# Revit family: Practibox_S_flush_mounting_cabinet_12_modules_réf_135361_to_135414
name_source: partatom
category: Equipement électrique
revit_build: Autodesk Revit 2018 (Build: 20170223_1515(x64)
units: mm (PartAtom-declared; Revit-internal decimal feet)

## family parameters
Basée sur le plan de construction = Non
Configuration du panneau = Deux colonnes, circuits au sein
Cote de connecteur circulaire = Utiliser le diamètre
Couper avec des vides une fois chargée = Non
Numéro OmniClass = 23.80.30.11.17
Partagée = Non
Point de calcul de pièce = Non
Titre OmniClass = Distribution Boards and Control Panels
Toujours verticalement = Oui
Type d'élément = Tableau de raccordement

## types (16) — shared parameters
Fabricant = "Legrand"
General Conditions of Use = https://export.legrand.com
URL = www.legrand.com
width = 328 mm  [stored 1.07612 ft]

## per-type parameters (varying)
| type | 1R | 2R | 3R | 4R | Ina | Terminal block E | Terminal block N | depth | door B 1 r | door B 2 r | door B 3 r | door B 4 r | door T 1 r | door T 2 r | door T 3 r | door T 4 r | door transparent | door white | height | size |
| Practibox_S_flush_mounting_cabinet_12_modules_135411 | Oui | Non | Non | Non | 63 A | 10 connections Icc 6kA | 10 connections Icc 6kA | 102 mm | Non | Non | Non | Non | Oui | Non | Non | Non | Oui | Non | 235 mm  [stored 0.770997 ft] | 1 row |
| Practibox_S_flush_mounting_cabinet_12_modules_135401 | Oui | Non | Non | Non | 63 A | 10 connections Icc 6kA | 10 connections Icc 6kA | 102 mm | Oui | Non | Non | Non | Non | Non | Non | Non | Non | Oui | 235 mm  [stored 0.770997 ft] | 1 row |
| Practibox_S_flush_mounting_cabinet_12_modules_135371 | Oui | Non | Non | Non | 63 A | 10 connections Icc 6kA | 10 connections Icc 6kA | 102 mm | Non | Non | Non | Non | Oui | Non | Non | Non | Oui | Non | 235 mm  [stored 0.770997 ft] | 1 row |
| Practibox_S_flush_mounting_cabinet_12_modules_135361 | Oui | Non | Non | Non | 63 A | 10 connections Icc 6kA | 10 connections Icc 6kA | 102 mm | Oui | Non | Non | Non | Non | Non | Non | Non | Non | Oui | 235 mm  [stored 0.770997 ft] | 1 row |
| Practibox_S_flush_mounting_cabinet_24_modules_135402 | Non | Oui | Non | Non | 90 A | 18 connections Icc 6kA | 20 connections Icc 6kA | 103 mm  [stored 0.337927 ft] | Non | Oui | Non | Non | Non | Non | Non | Non | Non | Oui | 385 mm  [stored 1.26312 ft] | 2 row |
| Practibox_S_flush_mounting_cabinet_24_modules_135412 | Non | Oui | Non | Non | 90 A | 18 connections Icc 6kA | 20 connections Icc 6kA | 103 mm  [stored 0.337927 ft] | Non | Non | Non | Non | Non | Oui | Non | Non | Oui | Non | 385 mm  [stored 1.26312 ft] | 2 row |
| Practibox_S_flush_mounting_cabinet_24_modules_135362 | Non | Oui | Non | Non | 90 A | 18 connections Icc 6kA | 18 connections Icc 6kA | 103 mm  [stored 0.337927 ft] | Non | Oui | Non | Non | Non | Non | Non | Non | Non | Oui | 385 mm  [stored 1.26312 ft] | 2 row |
| Practibox_S_flush_mounting_cabinet_24_modules_135372 | Non | Oui | Non | Non | 90 A | 18 connections Icc 6kA | 18 connections Icc 6kA | 103 mm  [stored 0.337927 ft] | Non | Non | Non | Non | Non | Oui | Non | Non | Oui | Non | 385 mm  [stored 1.26312 ft] | 2 row |
| Practibox_S_flush_mounting_cabinet_36_modules_135403 | Non | Non | Oui | Non | 90 A | 28 connections Icc 6kA | 20 connections Icc 6kA | 103 mm  [stored 0.337927 ft] | Non | Non | Oui | Non | Non | Non | Non | Non | Non | Oui | 535 mm  [stored 1.75525 ft] | 3 row |
| Practibox_S_flush_mounting_cabinet_36_modules_135413 | Non | Non | Oui | Non | 90 A | 28 connections Icc 6kA | 20 connections Icc 6kA | 103 mm  [stored 0.337927 ft] | Non | Non | Non | Non | Non | Non | Oui | Non | Oui | Non | 535 mm  [stored 1.75525 ft] | 3 row |
| Practibox_S_flush_mounting_cabinet_36_modules_135373 | Non | Non | Oui | Non | 90 A | 28 connections Icc 6kA | 20 connections Icc 6kA | 103 mm  [stored 0.337927 ft] | Non | Non | Non | Non | Non | Non | Oui | Non | Oui | Non | 535 mm  [stored 1.75525 ft] | 3 row |
| Practibox_S_flush_mounting_cabinet_36_modules_135363 | Non | Non | Oui | Non | 90 A | 28 connections Icc 6kA | 20 connections Icc 6kA | 103 mm  [stored 0.337927 ft] | Non | Non | Oui | Non | Non | Non | Non | Non | Non | Oui | 535 mm  [stored 1.75525 ft] | 3 row |
| Practibox_S_flush_mounting_cabinet_48_modules_135404 | Non | Non | Non | Oui | 90 A | 32 connections Icc 6kA | 20 connections Icc 6kA | 103 mm  [stored 0.337927 ft] | Non | Non | Non | Oui | Non | Non | Non | Non | Non | Oui | 765 mm  [stored 2.50984 ft] | 4 row |
| Practibox_S_flush_mounting_cabinet_48_modules_135414 | Non | Non | Non | Oui | 90 A | 32 connections Icc 6kA | 20 connections Icc 6kA | 103 mm  [stored 0.337927 ft] | Non | Non | Non | Non | Non | Non | Non | Oui | Oui | Non | 765 mm  [stored 2.50984 ft] | 4 row |
| Practibox_S_flush_mounting_cabinet_48_modules_135364 | Non | Non | Non | Oui | 90 A | 32 connections Icc 6kA | 20 connections Icc 6kA | 103 mm  [stored 0.337927 ft] | Non | Non | Non | Oui | Non | Non | Non | Non | Non | Oui | 765 mm  [stored 2.50984 ft] | 4 row |
| Practibox_S_flush_mounting_cabinet_48_modules_135374 | Non | Non | Non | Oui | 90 A | 32 connections Icc 6kA | 20 connections Icc 6kA | 103 mm  [stored 0.337927 ft] | Non | Non | Non | Non | Non | Non | Non | Oui | Oui | Non | 765 mm  [stored 2.50984 ft] | 4 row |

note: column(s) folded — value = type name in every type: Description

note: [stored X ft] marks values corroborated as IEEE doubles in the binary element streams (Revit-internal decimal feet)
